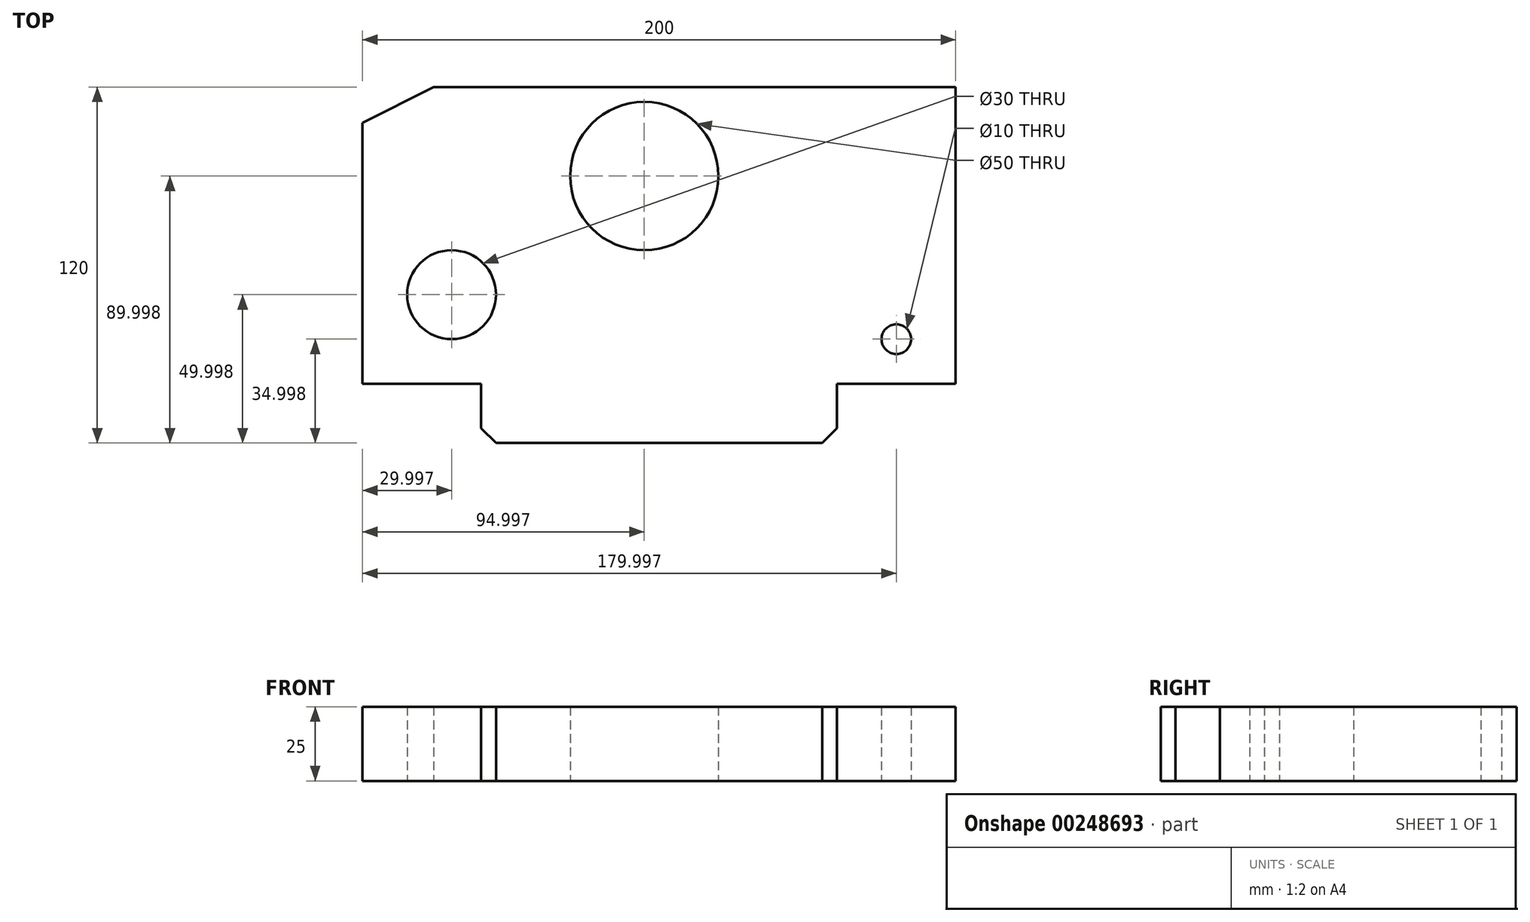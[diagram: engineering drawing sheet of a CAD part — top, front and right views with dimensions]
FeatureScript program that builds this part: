
annotation { "Feature Type Name" : "Feature", "Feature Type Description" : "" }
export const myFeature = defineFeature(function(context is Context, id is Id, definition is map)
    precondition{}
    {
        {
            var Q0;
            Q0=qCreatedBy(makeId("Top.planeOp"),FACE);
            var sketch = newSketch(context, id + "F0", { "sketchPlane" : qUnion([Q0])});
            skLineSegment(sketch, "E0", {"start": v(-68.18, -52.72) * mm, "end": v(-28.18, -52.72) * mm});
            skLineSegment(sketch, "E1", {"start": v(-28.18, -52.72) * mm, "end": v(-28.18, -72.72) * mm});
            skLineSegment(sketch, "E2", {"start": v(-28.18, -72.72) * mm, "end": v(91.82, -72.72) * mm});
            skLineSegment(sketch, "E3", {"start": v(91.82, -72.72) * mm, "end": v(91.82, -52.72) * mm});
            skLineSegment(sketch, "E4", {"start": v(91.82, -52.72) * mm, "end": v(131.82, -52.72) * mm});
            skLineSegment(sketch, "E5", {"start": v(131.82, -52.72) * mm, "end": v(131.82, 47.28) * mm});
            skLineSegment(sketch, "E6", {"start": v(131.82, 47.28) * mm, "end": v(-44.18, 47.28) * mm});
            skLineSegment(sketch, "E7", {"start": v(-68.18, 35.28) * mm, "end": v(-44.18, 47.28) * mm});
            skLineSegment(sketch, "E8", {"start": v(-68.18, 35.28) * mm, "end": v(-68.18, -22.72) * mm});
            skLineSegment(sketch, "E9", {"start": v(-68.18, -22.72) * mm, "end": v(-38.18, -22.72) * mm});
            skLineSegment(sketch, "E10", {"start": v(-44.18, 47.28) * mm, "end": v(26.82, 47.28) * mm});
            skLineSegment(sketch, "E11", {"start": v(26.82, 47.28) * mm, "end": v(26.82, 17.28) * mm});
            skLineSegment(sketch, "E12", {"start": v(-68.18, -22.72) * mm, "end": v(-68.18, -52.72) * mm});
            skLineSegment(sketch, "E13", {"start": v(131.82, -52.72) * mm, "end": v(111.82, -52.72) * mm});
            skLineSegment(sketch, "E14", {"start": v(111.82, -52.72) * mm, "end": v(111.82, -37.72) * mm});
            skCircle(sketch, "E15", {"center": v(26.82, 17.28) * mm, "radius": 25 * mm});
            skCircle(sketch, "E16", {"center": v(-38.18, -22.72) * mm, "radius": 15 * mm});
            skCircle(sketch, "E17", {"center": v(111.82, -37.72) * mm, "radius": 5 * mm});
            skSolve(sketch);
        }
        {
            var Q0;
            Q0 = qSketchRegion(id + "F0", true);
            extrude(context, id + "F1", {"entities" : qUnion([Q0]), "depth" : 25 * mm});
        }
        {
            var Q0;
            Q0=makeQuery(id+"F1.opExtrude","SWEPT_EDGE",EDGE,{"disambiguationData":[OSD([sQuery(id+"F0.wireOp",EDGE,"E1"),sQuery(id+"F0.wireOp",EDGE,"E2")])]});
            var Q1;
            Q1=makeQuery(id+"F1.opExtrude","SWEPT_EDGE",EDGE,{"disambiguationData":[OSD([sQuery(id+"F0.wireOp",EDGE,"E2"),sQuery(id+"F0.wireOp",EDGE,"E3")])]});
            chamfer(context, id + "F2", {"entities" : qUnion([Q0, Q1]), "chamferType" : ChamferType.OFFSET_ANGLE, "width" : 5 * mm, "oppositeDirection" : false, "angle" : 45 * degree, "tangentPropagation" : true});
        }
    });
